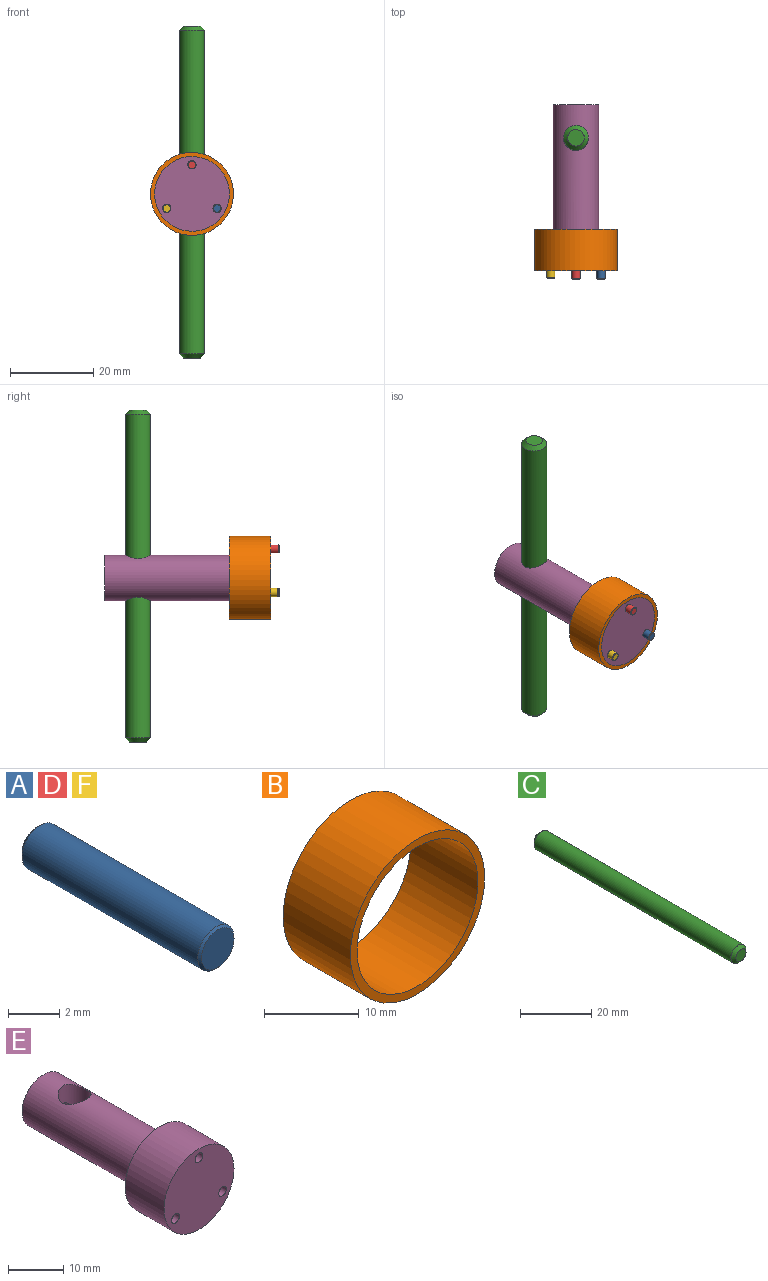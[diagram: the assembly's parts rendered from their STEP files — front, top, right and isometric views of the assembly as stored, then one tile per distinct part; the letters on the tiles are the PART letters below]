
ASSEMBLY  parts=6 mates=5
PART A: 5 faces, bbox 2x10x2 mm
  f0: cylinder r=1mm len=9.7mm, axis (0,1,0), area 60.9mm2, adj f3,f4
  f1: plane 1.8x1.8mm, normal (0,-1,0), area 2.5mm2, adj f4
  f2: plane 1.6x1.6mm, normal (0,1,0), area 2mm2, adj f3
  f3: cone r=1mm half-angle=45deg, axis (0,-1,0), area 1.6mm2, adj f0,f2
  f4: cone r=0.9mm half-angle=45deg, axis (0,1,0), area 0.8mm2, adj f0,f1
PART B: 4 faces, bbox 20x10x20 mm
  f0: cylinder r=9mm len=18mm, axis (0,1,0), area 565.5mm2, adj f2,f3
  f1: cylinder r=10mm len=20mm, axis (0,1,0), area 628.3mm2, adj f2,f3
  f2: plane 20x20mm, normal (0,-1,0), area 59.7mm2, adj f0,f1
  f3: plane 20x20mm, normal (0,1,0), area 59.7mm2, adj f0,f1
PART C: 5 faces, bbox 6x80x6 mm
  f0: cylinder r=3mm len=78mm, axis (0,1,0), area 1470.3mm2, adj f3,f4
  f1: plane 4x4mm, normal (0,-1,0), area 12.6mm2, adj f4
  f2: plane 4x4mm, normal (0,1,0), area 12.6mm2, adj f3
  f3: cone r=3mm half-angle=45deg, axis (0,-1,0), area 22.2mm2, adj f0,f2
  f4: cone r=2mm half-angle=45deg, axis (0,1,0), area 22.2mm2, adj f0,f1
PART D: same geometry as A
PART E: 16 faces, bbox 18x40x18 mm
  f0: cylinder r=3mm len=11mm, axis (0,0,1), area 182.6mm2, adj f9,f15
  f1: cylinder r=9mm len=18mm, axis (0,1,0), area 565.5mm2, adj f2,f10
  f2: plane 18x18mm, normal (0,-1,0), area 245mm2, adj f1,f3,f5,f7
  f3: cylinder r=1mm len=8mm, axis (0,-1,0), area 50.3mm2, adj f2,f4
  f4: plane 2x2mm, normal (0,-1,0), area 1.4mm2, adj f3,f12
  f5: cylinder r=1mm len=8mm, axis (0,-1,0), area 50.3mm2, adj f2,f6
  f6: plane 2x2mm, normal (0,-1,0), area 1.4mm2, adj f5,f14
  f7: cylinder r=1mm len=8mm, axis (0,-1,0), area 50.3mm2, adj f2,f8
  f8: plane 2x2mm, normal (0,-1,0), area 1.4mm2, adj f7,f13
  f9: cylinder r=5.5mm len=30mm, axis (0,1,0), area 977.9mm2, adj f0,f10,f11
  f10: plane 18x18mm, normal (0,1,0), area 154.1mm2, adj f1,f9,f12,f13,f14
  f11: plane 11x11mm, normal (0,1,0), area 87mm2, adj f9,f15
  f12: cylinder r=0.75mm len=2mm, axis (0,-1,0), area 9.4mm2, adj f4,f10
  f13: cylinder r=0.75mm len=2mm, axis (0,-1,0), area 9.4mm2, adj f8,f10
  f14: cylinder r=0.75mm len=2mm, axis (0,-1,0), area 9.4mm2, adj f6,f10
  f15: cylinder r=1.6mm len=5.46mm, axis (0,1,0), area 52.5mm2, adj f0,f11
PART F: same geometry as A
PLACE A t=(6.43,-15.85,-3.06)mm
PLACE B t=(0.37,-13.85,0.44)mm
PLACE C rot(axis=(1,0,0),90deg) t=(0.37,13.15,0.89)mm
PLACE D t=(0.37,-15.85,7.44)mm
PLACE E t=(0.37,1.15,0.44)mm fixed
PLACE F t=(-5.69,-15.65,-3.06)mm
MATE fastened A.f0 <-> E.f3  axis (0,1,0) through (6.43,-10.85,-3.06)mm
MATE slider C.f0 <-> E.f0  axis (0,0,1) through (0.37,13.15,0.89)mm
MATE fastened F.f0 <-> E.f5  axis (0,-1,0) through (-5.69,-10.85,-3.06)mm
MATE fastened B.f0 <-> E.f1  axis (0,1,0) through (0.37,-18.85,0.44)mm
MATE fastened D.f0 <-> E.f13  axis (0,1,0) through (0.37,-10.85,7.44)mm
